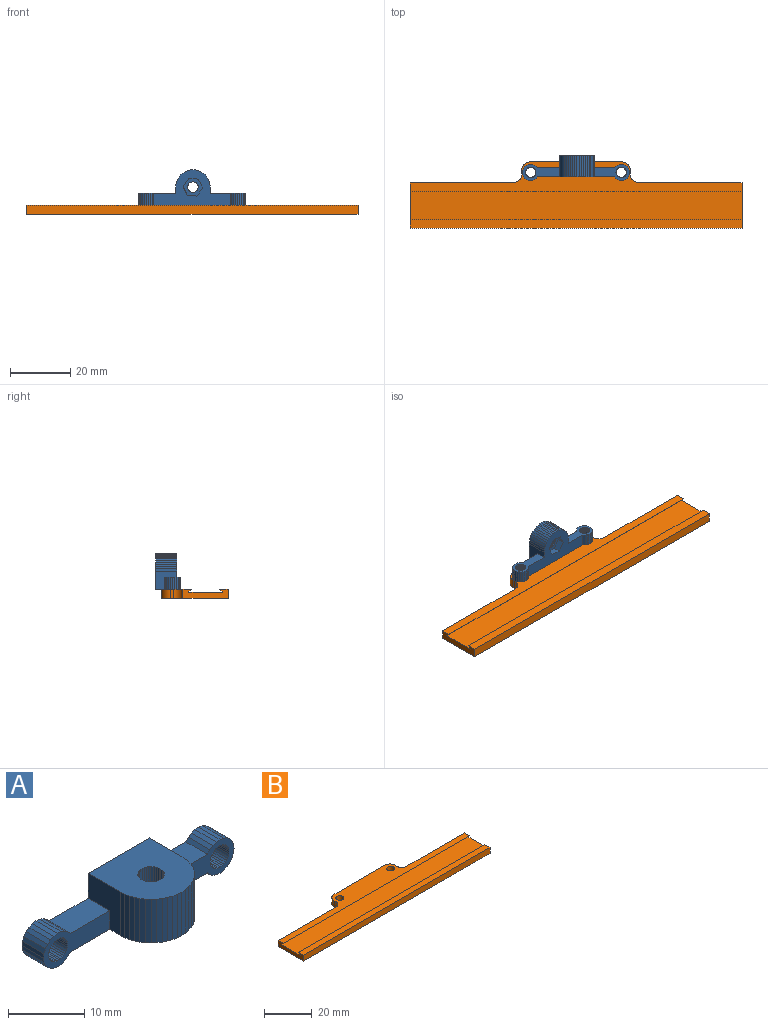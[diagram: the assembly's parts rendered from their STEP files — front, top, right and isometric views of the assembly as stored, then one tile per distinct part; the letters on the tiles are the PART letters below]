
ASSEMBLY  parts=2 mates=1
PART A: 195 faces, bbox 35.4x11.7x8.2 mm
  f0: plane 11.7x11.4mm, normal (0,0,1), area 109.7mm2, adj f1,f11,f12,f13,f14,f15,f16,f17
  f1: plane 7x0.67mm, normal (0.9,-0.44,0), area 5.2mm2, adj f0,f2,f30,f33
  f2: plane 25.51x11.7mm, normal (0,0,-1), area 148.3mm2, adj f1,f3,f4,f5,f7,f9,f10,f11
  f3: plane 2.25x2.24mm, normal (0.91,-0.42,0), area 2.5mm2, adj f2,f4,f5
  f4: plane 2.25x0.24mm, normal (0.91,-0.42,0), area 0.3mm2, adj f2,f3,f31
  f5: plane 2.95x2.25mm, normal (0.91,-0.42,0), area 4.5mm2, adj f2,f3,f6,f38
  f6: plane 6.47x5.9mm, normal (0,0,-1), area 17.9mm2, adj f5,f8,f10,f31,f34,f38,f84,f85
  f7: plane 2.6x2.25mm, normal (-0.91,0.42,0), area 3.2mm2, adj f2,f8,f34
  f8: plane 2.95x2.25mm, normal (-0.91,0.42,0), area 3.7mm2, adj f6,f7,f9
  f9: plane 2.25x0.35mm, normal (-0.91,0.42,0), area 0.4mm2, adj f2,f8,f10
  f10: plane 2.66x2.25mm, normal (-0.82,-0.58,0), area 7.3mm2, adj f2,f6,f9,f38
  f11: plane 35.4x8.2mm, normal (0,1,0), area 146.5mm2, adj f0,f2,f12,f39,f40,f41,f42,f43
  f12: plane 7x6mm, normal (1,0,0), area 30mm2, adj f0,f2,f11,f37,f50,f63
  f13: plane 7x0.67mm, normal (-0.44,-0.9,0), area 5.2mm2, adj f0,f2,f14,f15
  f14: plane 7x0.71mm, normal (-0.32,-0.95,0), area 5.2mm2, adj f0,f2,f13,f17
  f15: plane 7x0.62mm, normal (-0.56,-0.83,0), area 5.2mm2, adj f0,f2,f13,f18
  f16: plane 7x0.67mm, normal (0.44,-0.9,0), area 5.2mm2, adj f0,f2,f20,f21
  f17: plane 7x0.73mm, normal (-0.2,-0.98,0), area 5.2mm2, adj f0,f2,f14,f22
  f18: plane 7x0.56mm, normal (-0.66,-0.75,0), area 5.2mm2, adj f0,f2,f15,f23
  f19: plane 7x0.67mm, normal (-0.9,-0.44,0), area 5.2mm2, adj f0,f2,f24,f28
  f20: plane 7x0.62mm, normal (0.56,-0.83,0), area 5.2mm2, adj f0,f2,f16,f25
  f21: plane 7x0.71mm, normal (0.32,-0.95,0), area 5.2mm2, adj f0,f2,f16,f26
  f22: plane 7x0.74mm, normal (-0.07,-1,0), area 5.2mm2, adj f0,f2,f17,f27
  f23: plane 7x0.56mm, normal (-0.75,-0.66,0), area 5.2mm2, adj f0,f2,f18,f24
  f24: plane 7x0.62mm, normal (-0.83,-0.56,0), area 5.2mm2, adj f0,f2,f19,f23
  f25: plane 7x0.56mm, normal (0.66,-0.75,0), area 5.2mm2, adj f0,f2,f20,f29
  f26: plane 7x0.73mm, normal (0.2,-0.98,0), area 5.2mm2, adj f0,f2,f21,f27
  f27: plane 7x0.74mm, normal (0.07,-1,0), area 5.2mm2, adj f0,f2,f22,f26
  f28: plane 7x0.71mm, normal (-0.95,-0.32,0), area 5.2mm2, adj f0,f2,f19,f32
  f29: plane 7x0.56mm, normal (0.75,-0.66,0), area 5.2mm2, adj f0,f2,f25,f30
  f30: plane 7x0.62mm, normal (0.83,-0.56,0), area 5.2mm2, adj f0,f1,f2,f29
  f31: plane 2.66x2.25mm, normal (0.82,0.58,0), area 7.3mm2, adj f2,f4,f6,f34
  f32: plane 7x0.73mm, normal (-0.98,-0.2,0), area 5.2mm2, adj f0,f2,f28,f35
  f33: plane 7x0.71mm, normal (0.95,-0.32,0), area 5.2mm2, adj f0,f1,f2,f36
  f34: plane 3.24x2.25mm, normal (-0.09,1,0), area 7.3mm2, adj f2,f6,f7,f31
  f35: plane 7x0.74mm, normal (-1,-0.07,0), area 5.2mm2, adj f0,f2,f32,f39
  f36: plane 7x0.73mm, normal (0.98,-0.2,0), area 5.2mm2, adj f0,f2,f33,f37
  f37: plane 7x0.74mm, normal (1,-0.07,0), area 5.2mm2, adj f0,f2,f12,f36
  f38: plane 3.24x2.25mm, normal (0.09,-1,0), area 7.3mm2, adj f2,f5,f6,f10
  f39: plane 7x6mm, normal (-1,0,0), area 30mm2, adj f0,f2,f11,f35,f49,f62
  f40: plane 4x0.64mm, normal (-0.93,0,-0.37), area 2.7mm2, adj f11,f41,f61,f62
  f41: plane 4x0.55mm, normal (-0.8,0,-0.6), area 2.7mm2, adj f11,f40,f42,f62
  f42: plane 4x0.54mm, normal (-0.63,0,-0.78), area 2.7mm2, adj f11,f41,f43,f62
  f43: plane 4x0.63mm, normal (-0.41,0,-0.91), area 2.7mm2, adj f11,f42,f44,f62
  f44: plane 4x0.68mm, normal (-0.17,0,-0.99), area 2.7mm2, adj f11,f43,f45,f62
  f45: plane 4x0.68mm, normal (0.09,0,-1), area 2.7mm2, adj f11,f44,f46,f62
  f46: plane 4x0.65mm, normal (0.34,0,-0.94), area 2.7mm2, adj f11,f45,f47,f62
  f47: plane 4x0.57mm, normal (0.56,0,-0.83), area 2.7mm2, adj f11,f46,f48,f62
  f48: plane 4x0.52mm, normal (0.75,0,-0.66), area 2.7mm2, adj f2,f11,f47,f62
  f49: plane 7.36x4mm, normal (0,0,1), area 29.4mm2, adj f11,f39,f51,f62
  f50: plane 6.76x4mm, normal (0,0,1), area 27mm2, adj f11,f12,f63,f71
  f51: plane 4x0.52mm, normal (0.75,0,0.66), area 2.7mm2, adj f11,f49,f52,f62
  f52: plane 4x0.57mm, normal (0.56,0,0.83), area 2.7mm2, adj f11,f51,f53,f62
  f53: plane 4x0.65mm, normal (0.34,0,0.94), area 2.7mm2, adj f11,f52,f54,f62
  f54: plane 4x0.68mm, normal (0.09,0,1), area 2.7mm2, adj f11,f53,f55,f62
  f55: plane 4x0.68mm, normal (-0.17,0,0.99), area 2.7mm2, adj f11,f54,f56,f62
  f56: plane 4x0.63mm, normal (-0.41,0,0.91), area 2.7mm2, adj f11,f55,f57,f62
  f57: plane 4x0.54mm, normal (-0.63,0,0.78), area 2.7mm2, adj f11,f56,f58,f62
  f58: plane 4x0.55mm, normal (-0.8,0,0.6), area 2.7mm2, adj f11,f57,f59,f62
  f59: plane 4x0.64mm, normal (-0.93,0,0.37), area 2.7mm2, adj f11,f58,f60,f62
  f60: plane 4x0.68mm, normal (-0.99,0,0.13), area 2.7mm2, adj f11,f59,f61,f62
  f61: plane 4x0.68mm, normal (-0.99,0,-0.13), area 2.7mm2, adj f11,f40,f60,f62
  f62: plane 12.3x5.4mm, normal (0,-1,0), area 34.3mm2, adj f2,f39,f40,f41,f42,f43,f44,f45
  f63: plane 11.7x5.4mm, normal (0,-1,0), area 32.5mm2, adj f2,f12,f50,f64,f65,f66,f67,f68
  f64: plane 4x0.55mm, normal (0.8,0,0.6), area 2.7mm2, adj f11,f63,f65,f83
  f65: plane 4x0.54mm, normal (0.63,0,0.78), area 2.7mm2, adj f11,f63,f64,f66
  f66: plane 4x0.63mm, normal (0.41,0,0.91), area 2.7mm2, adj f11,f63,f65,f67
  f67: plane 4x0.68mm, normal (0.17,0,0.99), area 2.7mm2, adj f11,f63,f66,f68
  f68: plane 4x0.68mm, normal (-0.09,0,1), area 2.7mm2, adj f11,f63,f67,f69
  f69: plane 4x0.65mm, normal (-0.34,0,0.94), area 2.7mm2, adj f11,f63,f68,f70
  f70: plane 4x0.57mm, normal (-0.56,0,0.83), area 2.7mm2, adj f11,f63,f69,f71
  f71: plane 4x0.52mm, normal (-0.75,0,0.66), area 2.7mm2, adj f11,f50,f63,f70
  f72: plane 4x0.52mm, normal (-0.75,0,-0.66), area 2.7mm2, adj f2,f11,f63,f73
  f73: plane 4x0.57mm, normal (-0.56,0,-0.83), area 2.7mm2, adj f11,f63,f72,f74
  f74: plane 4x0.65mm, normal (-0.34,0,-0.94), area 2.7mm2, adj f11,f63,f73,f75
  f75: plane 4x0.68mm, normal (-0.09,0,-1), area 2.7mm2, adj f11,f63,f74,f76
  f76: plane 4x0.68mm, normal (0.17,0,-0.99), area 2.7mm2, adj f11,f63,f75,f77
  f77: plane 4x0.63mm, normal (0.41,0,-0.91), area 2.7mm2, adj f11,f63,f76,f78
  f78: plane 4x0.54mm, normal (0.63,0,-0.78), area 2.7mm2, adj f11,f63,f77,f79
  f79: plane 4x0.55mm, normal (0.8,0,-0.6), area 2.7mm2, adj f11,f63,f78,f80
  f80: plane 4x0.64mm, normal (0.93,0,-0.37), area 2.7mm2, adj f11,f63,f79,f81
  f81: plane 4x0.68mm, normal (0.99,0,-0.13), area 2.7mm2, adj f11,f63,f80,f82
  f82: plane 4x0.68mm, normal (0.99,0,0.13), area 2.7mm2, adj f11,f63,f81,f83
  f83: plane 4x0.64mm, normal (0.93,0,0.37), area 2.7mm2, adj f11,f63,f64,f82
  f84: plane 4.75x0.3mm, normal (0.08,1,0), area 1.4mm2, adj f0,f6,f85,f120
  f85: plane 4.75x0.3mm, normal (-0.08,1,0), area 1.4mm2, adj f0,f6,f84,f86
  f86: plane 4.75x0.29mm, normal (-0.25,0.97,0), area 1.4mm2, adj f0,f6,f85,f87
  f87: plane 4.75x0.27mm, normal (-0.41,0.91,0), area 1.4mm2, adj f0,f6,f86,f88
  f88: plane 4.75x0.25mm, normal (-0.56,0.83,0), area 1.4mm2, adj f0,f6,f87,f89
  f89: plane 4.75x0.21mm, normal (-0.69,0.72,0), area 1.4mm2, adj f0,f6,f88,f90
  f90: plane 4.75x0.24mm, normal (-0.8,0.59,0), area 1.4mm2, adj f0,f6,f89,f91
  f91: plane 4.75x0.27mm, normal (-0.89,0.45,0), area 1.4mm2, adj f0,f6,f90,f92
  f92: plane 4.75x0.28mm, normal (-0.96,0.29,0), area 1.4mm2, adj f0,f6,f91,f93
  f93: plane 4.75x0.29mm, normal (-0.99,0.13,0), area 1.4mm2, adj f0,f6,f92,f94
  f94: plane 4.75x0.3mm, normal (-1,-0.04,0), area 1.4mm2, adj f0,f6,f93,f95
  f95: plane 4.75x0.29mm, normal (-0.98,-0.21,0), area 1.4mm2, adj f0,f6,f94,f96
  f96: plane 4.75x0.28mm, normal (-0.93,-0.37,0), area 1.4mm2, adj f0,f6,f95,f97
  f97: plane 4.75x0.25mm, normal (-0.85,-0.52,0), area 1.4mm2, adj f0,f6,f96,f98
  f98: plane 4.75x0.22mm, normal (-0.75,-0.66,0), area 1.4mm2, adj f0,f6,f97,f99
  f99: plane 4.75x0.23mm, normal (-0.63,-0.78,0), area 1.4mm2, adj f0,f6,f98,f100
  f100: plane 4.75x0.26mm, normal (-0.49,-0.87,0), area 1.4mm2, adj f0,f6,f99,f101
  f101: plane 4.75x0.28mm, normal (-0.33,-0.94,0), area 1.4mm2, adj f0,f6,f100,f102
  f102: plane 4.75x0.29mm, normal (-0.17,-0.99,0), area 1.4mm2, adj f0,f6,f101,f103
  f103: plane 4.75x0.3mm, normal (0,-1,0), area 1.4mm2, adj f0,f6,f102,f104
  f104: plane 4.75x0.29mm, normal (0.17,-0.99,0), area 1.4mm2, adj f0,f6,f103,f105
  f105: plane 4.75x0.28mm, normal (0.33,-0.94,0), area 1.4mm2, adj f0,f6,f104,f106
  f106: plane 4.75x0.26mm, normal (0.49,-0.87,0), area 1.4mm2, adj f0,f6,f105,f107
  f107: plane 4.75x0.23mm, normal (0.63,-0.78,0), area 1.4mm2, adj f0,f6,f106,f108
  f108: plane 4.75x0.22mm, normal (0.75,-0.66,0), area 1.4mm2, adj f0,f6,f107,f109
  f109: plane 4.75x0.25mm, normal (0.85,-0.52,0), area 1.4mm2, adj f0,f6,f108,f110
  f110: plane 4.75x0.28mm, normal (0.93,-0.37,0), area 1.4mm2, adj f0,f6,f109,f111
  f111: plane 4.75x0.29mm, normal (0.98,-0.21,0), area 1.4mm2, adj f0,f6,f110,f112
  f112: plane 4.75x0.3mm, normal (1,-0.04,0), area 1.4mm2, adj f0,f6,f111,f113
  f113: plane 4.75x0.29mm, normal (0.99,0.13,0), area 1.4mm2, adj f0,f6,f112,f114
  f114: plane 4.75x0.28mm, normal (0.96,0.29,0), area 1.4mm2, adj f0,f6,f113,f115
  f115: plane 4.75x0.27mm, normal (0.89,0.45,0), area 1.4mm2, adj f0,f6,f114,f116
  f116: plane 4.75x0.24mm, normal (0.8,0.59,0), area 1.4mm2, adj f0,f6,f115,f117
  f117: plane 4.75x0.21mm, normal (0.69,0.72,0), area 1.4mm2, adj f0,f6,f116,f118
  f118: plane 4.75x0.25mm, normal (0.56,0.83,0), area 1.4mm2, adj f0,f6,f117,f119
  f119: plane 4.75x0.27mm, normal (0.41,0.91,0), area 1.4mm2, adj f0,f6,f118,f120
  f120: plane 4.75x0.29mm, normal (0.25,0.97,0), area 1.4mm2, adj f0,f6,f84,f119
  f121: plane 4x0.3mm, normal (1,0,0.08), area 1.2mm2, adj f11,f63,f122,f157
  f122: plane 4x0.3mm, normal (1,0,-0.08), area 1.2mm2, adj f11,f63,f121,f123
  f123: plane 4x0.29mm, normal (0.97,0,-0.25), area 1.2mm2, adj f11,f63,f122,f124
  f124: plane 4x0.27mm, normal (0.91,0,-0.41), area 1.2mm2, adj f11,f63,f123,f125
  f125: plane 4x0.25mm, normal (0.83,0,-0.56), area 1.2mm2, adj f11,f63,f124,f126
  f126: plane 4x0.21mm, normal (0.72,0,-0.69), area 1.2mm2, adj f11,f63,f125,f127
  f127: plane 4x0.24mm, normal (0.59,0,-0.8), area 1.2mm2, adj f11,f63,f126,f128
  f128: plane 4x0.27mm, normal (0.45,0,-0.89), area 1.2mm2, adj f11,f63,f127,f129
  f129: plane 4x0.28mm, normal (0.29,0,-0.96), area 1.2mm2, adj f11,f63,f128,f130
  f130: plane 4x0.29mm, normal (0.13,0,-0.99), area 1.2mm2, adj f11,f63,f129,f131
  f131: plane 4x0.3mm, normal (-0.04,0,-1), area 1.2mm2, adj f11,f63,f130,f132
  f132: plane 4x0.29mm, normal (-0.21,0,-0.98), area 1.2mm2, adj f11,f63,f131,f133
  f133: plane 4x0.28mm, normal (-0.37,0,-0.93), area 1.2mm2, adj f11,f63,f132,f134
  f134: plane 4x0.25mm, normal (-0.52,0,-0.85), area 1.2mm2, adj f11,f63,f133,f135
  f135: plane 4x0.22mm, normal (-0.66,0,-0.75), area 1.2mm2, adj f11,f63,f134,f136
  f136: plane 4x0.23mm, normal (-0.78,0,-0.63), area 1.2mm2, adj f11,f63,f135,f137
  f137: plane 4x0.26mm, normal (-0.87,0,-0.49), area 1.2mm2, adj f11,f63,f136,f138
  f138: plane 4x0.28mm, normal (-0.94,0,-0.33), area 1.2mm2, adj f11,f63,f137,f139
  f139: plane 4x0.29mm, normal (-0.99,0,-0.17), area 1.2mm2, adj f11,f63,f138,f140
  f140: plane 4x0.3mm, normal (-1,0,0), area 1.2mm2, adj f11,f63,f139,f141
  f141: plane 4x0.29mm, normal (-0.99,0,0.17), area 1.2mm2, adj f11,f63,f140,f142
  f142: plane 4x0.28mm, normal (-0.94,0,0.33), area 1.2mm2, adj f11,f63,f141,f143
  f143: plane 4x0.26mm, normal (-0.87,0,0.49), area 1.2mm2, adj f11,f63,f142,f144
  f144: plane 4x0.23mm, normal (-0.78,0,0.63), area 1.2mm2, adj f11,f63,f143,f145
  f145: plane 4x0.22mm, normal (-0.66,0,0.75), area 1.2mm2, adj f11,f63,f144,f146
  f146: plane 4x0.25mm, normal (-0.52,0,0.85), area 1.2mm2, adj f11,f63,f145,f147
  f147: plane 4x0.28mm, normal (-0.37,0,0.93), area 1.2mm2, adj f11,f63,f146,f148
  f148: plane 4x0.29mm, normal (-0.21,0,0.98), area 1.2mm2, adj f11,f63,f147,f149
  f149: plane 4x0.3mm, normal (-0.04,0,1), area 1.2mm2, adj f11,f63,f148,f150
  f150: plane 4x0.29mm, normal (0.13,0,0.99), area 1.2mm2, adj f11,f63,f149,f151
  f151: plane 4x0.28mm, normal (0.29,0,0.96), area 1.2mm2, adj f11,f63,f150,f152
  f152: plane 4x0.27mm, normal (0.45,0,0.89), area 1.2mm2, adj f11,f63,f151,f153
  f153: plane 4x0.24mm, normal (0.59,0,0.8), area 1.2mm2, adj f11,f63,f152,f154
  f154: plane 4x0.21mm, normal (0.72,0,0.69), area 1.2mm2, adj f11,f63,f153,f155
  f155: plane 4x0.25mm, normal (0.83,0,0.56), area 1.2mm2, adj f11,f63,f154,f156
  f156: plane 4x0.27mm, normal (0.91,0,0.41), area 1.2mm2, adj f11,f63,f155,f157
  f157: plane 4x0.29mm, normal (0.97,0,0.25), area 1.2mm2, adj f11,f63,f121,f156
  f158: plane 4x0.3mm, normal (1,0,0.08), area 1.2mm2, adj f11,f62,f159,f194
  f159: plane 4x0.3mm, normal (1,0,-0.08), area 1.2mm2, adj f11,f62,f158,f160
  f160: plane 4x0.29mm, normal (0.97,0,-0.25), area 1.2mm2, adj f11,f62,f159,f161
  f161: plane 4x0.27mm, normal (0.91,0,-0.41), area 1.2mm2, adj f11,f62,f160,f162
  f162: plane 4x0.25mm, normal (0.83,0,-0.56), area 1.2mm2, adj f11,f62,f161,f163
  f163: plane 4x0.21mm, normal (0.72,0,-0.69), area 1.2mm2, adj f11,f62,f162,f164
  f164: plane 4x0.24mm, normal (0.59,0,-0.8), area 1.2mm2, adj f11,f62,f163,f165
  f165: plane 4x0.27mm, normal (0.45,0,-0.89), area 1.2mm2, adj f11,f62,f164,f166
  f166: plane 4x0.28mm, normal (0.29,0,-0.96), area 1.2mm2, adj f11,f62,f165,f167
  f167: plane 4x0.29mm, normal (0.13,0,-0.99), area 1.2mm2, adj f11,f62,f166,f168
  f168: plane 4x0.3mm, normal (-0.04,0,-1), area 1.2mm2, adj f11,f62,f167,f169
  f169: plane 4x0.29mm, normal (-0.21,0,-0.98), area 1.2mm2, adj f11,f62,f168,f170
  f170: plane 4x0.28mm, normal (-0.37,0,-0.93), area 1.2mm2, adj f11,f62,f169,f171
  f171: plane 4x0.25mm, normal (-0.52,0,-0.85), area 1.2mm2, adj f11,f62,f170,f172
  f172: plane 4x0.22mm, normal (-0.66,0,-0.75), area 1.2mm2, adj f11,f62,f171,f173
  f173: plane 4x0.23mm, normal (-0.78,0,-0.63), area 1.2mm2, adj f11,f62,f172,f174
  f174: plane 4x0.26mm, normal (-0.87,0,-0.49), area 1.2mm2, adj f11,f62,f173,f175
  f175: plane 4x0.28mm, normal (-0.94,0,-0.33), area 1.2mm2, adj f11,f62,f174,f176
  f176: plane 4x0.29mm, normal (-0.99,0,-0.17), area 1.2mm2, adj f11,f62,f175,f177
  f177: plane 4x0.3mm, normal (-1,0,0), area 1.2mm2, adj f11,f62,f176,f178
  f178: plane 4x0.29mm, normal (-0.99,0,0.17), area 1.2mm2, adj f11,f62,f177,f179
  f179: plane 4x0.28mm, normal (-0.94,0,0.33), area 1.2mm2, adj f11,f62,f178,f180
  f180: plane 4x0.26mm, normal (-0.87,0,0.49), area 1.2mm2, adj f11,f62,f179,f181
  f181: plane 4x0.23mm, normal (-0.78,0,0.63), area 1.2mm2, adj f11,f62,f180,f182
  f182: plane 4x0.22mm, normal (-0.66,0,0.75), area 1.2mm2, adj f11,f62,f181,f183
  f183: plane 4x0.25mm, normal (-0.52,0,0.85), area 1.2mm2, adj f11,f62,f182,f184
  f184: plane 4x0.28mm, normal (-0.37,0,0.93), area 1.2mm2, adj f11,f62,f183,f185
  f185: plane 4x0.29mm, normal (-0.21,0,0.98), area 1.2mm2, adj f11,f62,f184,f186
  f186: plane 4x0.3mm, normal (-0.04,0,1), area 1.2mm2, adj f11,f62,f185,f187
  f187: plane 4x0.29mm, normal (0.13,0,0.99), area 1.2mm2, adj f11,f62,f186,f188
  f188: plane 4x0.28mm, normal (0.29,0,0.96), area 1.2mm2, adj f11,f62,f187,f189
  f189: plane 4x0.27mm, normal (0.45,0,0.89), area 1.2mm2, adj f11,f62,f188,f190
  f190: plane 4x0.24mm, normal (0.59,0,0.8), area 1.2mm2, adj f11,f62,f189,f191
  f191: plane 4x0.21mm, normal (0.72,0,0.69), area 1.2mm2, adj f11,f62,f190,f192
  f192: plane 4x0.25mm, normal (0.83,0,0.56), area 1.2mm2, adj f11,f62,f191,f193
  f193: plane 4x0.27mm, normal (0.91,0,0.41), area 1.2mm2, adj f11,f62,f192,f194
  f194: plane 4x0.29mm, normal (0.97,0,0.25), area 1.2mm2, adj f11,f62,f158,f193
PART B: 22 faces, bbox 110x22x3 mm
  f0: plane 34x3mm, normal (0,1,0), area 102mm2, adj f1,f4,f7,f21
  f1: plane 110x9.95mm, normal (0,0,1), area 559.4mm2, adj f0,f2,f3,f4,f12,f13,f14,f15
  f2: plane 15x3mm, normal (1,0,0), area 34.9mm2, adj f1,f3,f5,f6,f7,f8,f9,f10
  f3: plane 34x3mm, normal (0,1,0), area 102mm2, adj f1,f2,f7,f20
  f4: plane 15x3mm, normal (-1,0,0), area 34.9mm2, adj f0,f1,f5,f6,f7,f8,f9,f10
  f5: plane 110x3mm, normal (0,-1,0), area 330mm2, adj f2,f4,f6,f7
  f6: plane 110x2.95mm, normal (0,0,1), area 324.5mm2, adj f2,f4,f5,f11
  f7: plane 110x22mm, normal (0,0,-1), area 1884.9mm2, adj f0,f2,f3,f4,f5,f13,f14,f15
  f8: plane 110x0.05mm, normal (0,-1,0), area 5.5mm2, adj f2,f4,f10,f12
  f9: plane 110x0.05mm, normal (0,1,0), area 5.5mm2, adj f2,f4,f10,f11
  f10: plane 110x11mm, normal (0,0,1), area 1210mm2, adj f2,f4,f8,f9
  f11: plane 110x0.95mm, normal (0,0.71,-0.71), area 147.8mm2, adj f2,f4,f6,f9
  f12: plane 110x0.95mm, normal (0,-0.71,-0.71), area 147.8mm2, adj f1,f2,f4,f8
  f13: plane 3x1mm, normal (1,0,0), area 3mm2, adj f1,f7,f18,f20
  f14: plane 3x1mm, normal (-1,0,0), area 3mm2, adj f1,f7,f19,f21
  f15: plane 30x3mm, normal (0,1,0), area 90mm2, adj f1,f7,f18,f19
  f16: cylinder r=1.65mm len=3.3mm, axis (0,0,1), area 31.1mm2, adj f1,f7
  f17: cylinder r=1.65mm len=3.3mm, axis (0,0,1), area 31.1mm2, adj f1,f7
  f18: cylinder r=3mm len=3mm, axis (0,0,1), area 14.1mm2, adj f1,f7,f13,f15
  f19: cylinder r=3mm len=3mm, axis (0,0,-1), area 14.1mm2, adj f1,f7,f14,f15
  f20: cylinder r=3mm len=3mm, axis (0,0,-1), area 14.1mm2, adj f1,f3,f7,f13
  f21: cylinder r=3mm len=3mm, axis (0,0,1), area 14.1mm2, adj f0,f1,f7,f14
PLACE A rot(axis=(-1,0,0),90deg) t=(-17.7,-90.5,-6)mm
PLACE B at identity
MATE fastened A.f11 <-> B.f16  axis (0,0,-1) through (-15,11,3)mm
